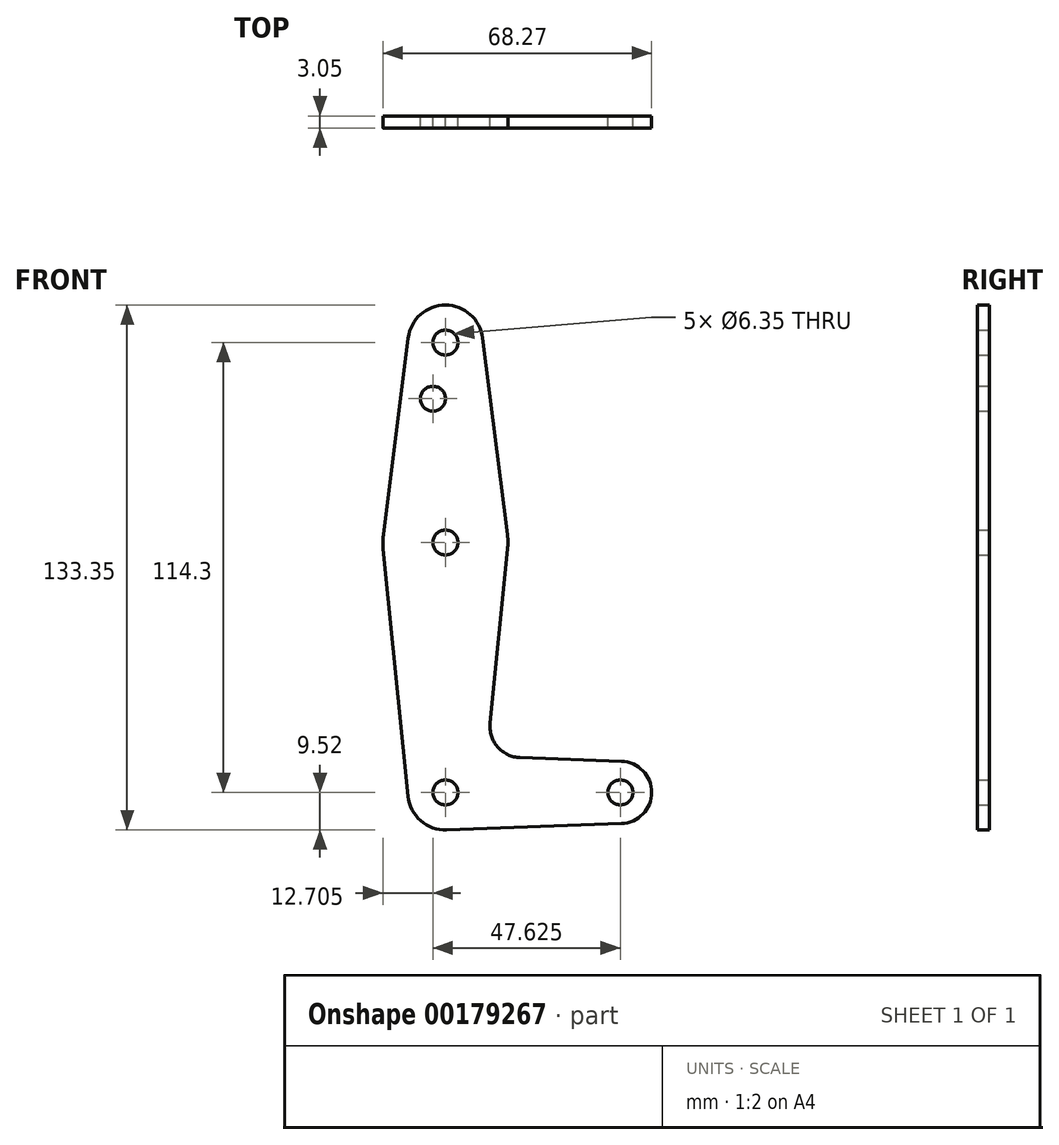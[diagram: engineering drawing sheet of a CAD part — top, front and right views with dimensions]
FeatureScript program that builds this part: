
annotation { "Feature Type Name" : "Feature", "Feature Type Description" : "" }
export const myFeature = defineFeature(function(context is Context, id is Id, definition is map)
    precondition{}
    {
        {
            var Q0;
            Q0=qCreatedBy(makeId("Front.planeOp"),FACE);
            var sketch = newSketch(context, id + "F0", { "sketchPlane" : qUnion([Q0])});
            skLineSegment(sketch, "E0", {"start": v(0, 114.3) * mm, "end": v(0, 0) * mm, "construction": true});
            skLineSegment(sketch, "E1", {"start": v(0, 0) * mm, "end": v(44.45, 0) * mm, "construction": true});
            skCircle(sketch, "E2", {"center": v(0, 114.3) * mm, "radius": 9.53 * mm});
            skCircle(sketch, "E3", {"center": v(0, 63.5) * mm, "radius": 15.88 * mm});
            skCircle(sketch, "E4", {"center": v(0, 0) * mm, "radius": 9.53 * mm});
            skCircle(sketch, "E5", {"center": v(44.45, 0) * mm, "radius": 7.94 * mm});
            skLineSegment(sketch, "E6", {"start": v(-9.45, 115.5) * mm, "end": v(-15.75, 65.48) * mm});
            skLineSegment(sketch, "E7", {"start": v(9.45, 115.5) * mm, "end": v(15.75, 65.48) * mm});
            skLineSegment(sketch, "E8", {"start": v(15.8, 61.91) * mm, "end": v(11.34, 17.6) * mm});
            skLineSegment(sketch, "E9", {"start": v(18.97, 8.85) * mm, "end": v(44.73, 7.93) * mm});
            skLineSegment(sketch, "E10", {"start": v(0.34, -9.52) * mm, "end": v(44.73, -7.93) * mm});
            skLineSegment(sketch, "E11", {"start": v(-15.8, 61.91) * mm, "end": v(-9.48, -0.95) * mm});
            skCircle(sketch, "E12", {"center": v(0, 114.3) * mm, "radius": 3.18 * mm});
            skCircle(sketch, "E13", {"center": v(-3.17, 100.03) * mm, "radius": 3.18 * mm});
            skCircle(sketch, "E14", {"center": v(0, 63.5) * mm, "radius": 3.18 * mm});
            skCircle(sketch, "E15", {"center": v(0, 0) * mm, "radius": 3.18 * mm});
            skCircle(sketch, "E16", {"center": v(44.45, 0) * mm, "radius": 3.18 * mm});
            skArc(sketch, "E17.filletArc", {"start": v(11.34, 17.6) * mm, "mid": v(13.26, 11.57) * mm, "end": v(18.97, 8.85) * mm});
            skSolve(sketch);
        }
        {
            var Q0;
            Q0 = qSketchRegion(id + "F0", true);
            extrude(context, id + "F1", {"entities" : qUnion([Q0]), "depth" : 3.05 * mm});
        }
    });
